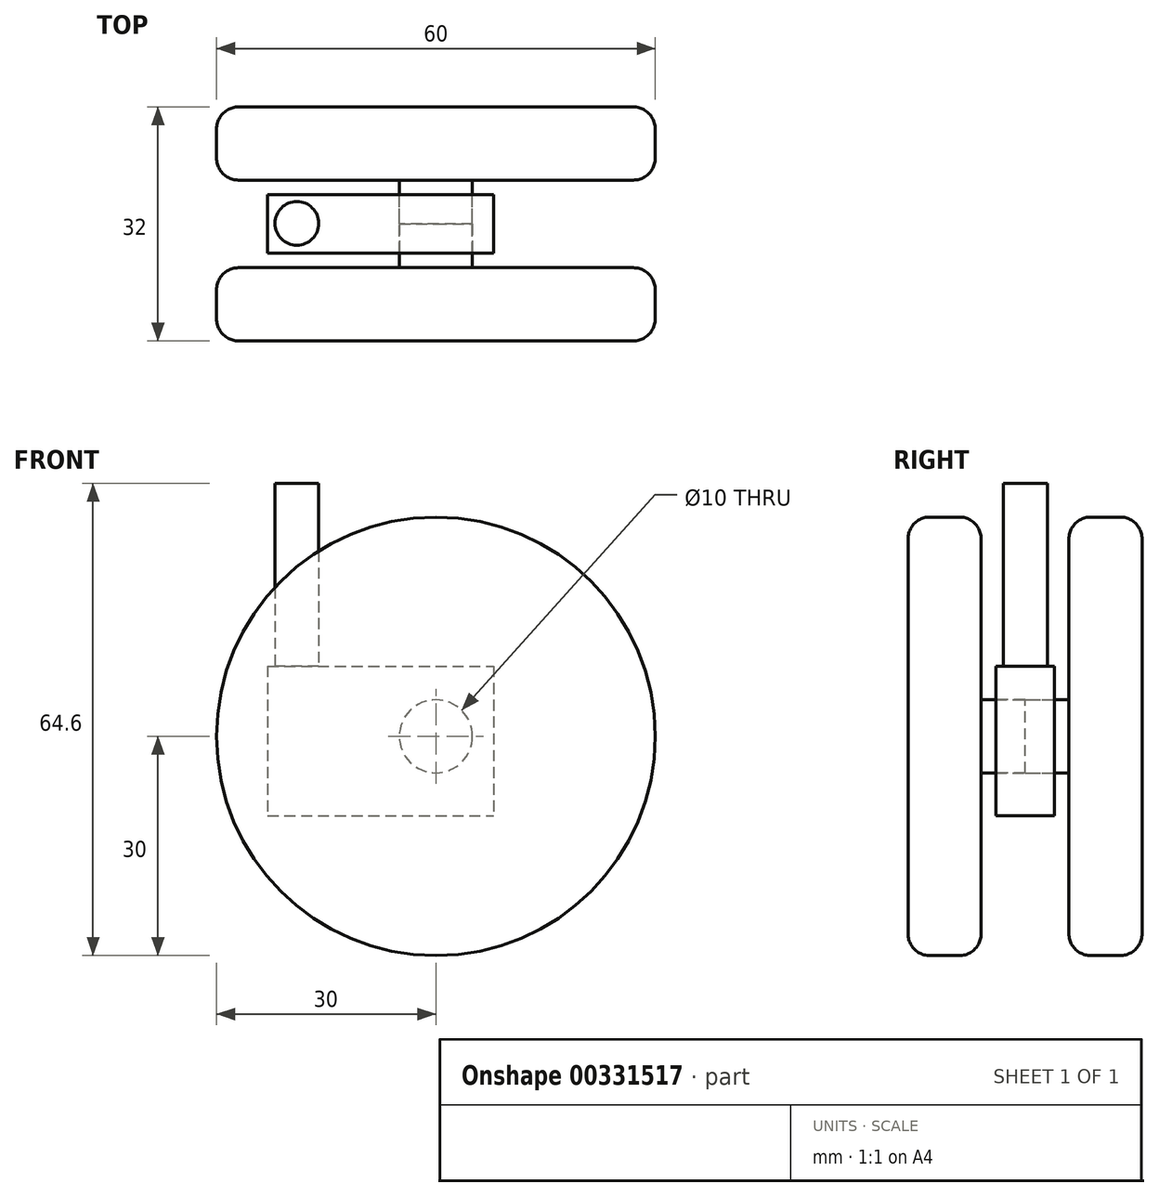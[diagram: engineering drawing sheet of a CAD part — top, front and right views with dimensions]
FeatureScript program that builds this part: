
annotation { "Feature Type Name" : "Feature", "Feature Type Description" : "" }
export const myFeature = defineFeature(function(context is Context, id is Id, definition is map)
    precondition{}
    {
        {
            var Q0;
            Q0=qCreatedBy(makeId("Front.planeOp"),FACE);
            var sketch = newSketch(context, id + "F0", { "sketchPlane" : qUnion([Q0])});
            skCircle(sketch, "E0", {"center": v(0, 0) * mm, "radius": 30 * mm});
            skSolve(sketch);
        }
        {
            var Q0;
            Q0=makeQuery(id+"F0.imprint","IMPRINT",FACE,{"disambiguationData":[TD([[makeQuery(id+"F0.imprint","IMPRINT",EDGE,{"derivedFrom":sQuery(id+"F0.wireOp",EDGE,"E0")}),1.0]])]});
            extrude(context, id + "F1", {"entities" : qUnion([Q0]), "depth" : 10 * mm});
        }
        {
            var Q0;
            Q0=makeQuery(id+"F1.opExtrude","CAP_EDGE",EDGE,{"disambiguationData":[OSD([sQuery(id+"F0.wireOp",EDGE,"E0")])],"isStart":false});
            var Q1;
            Q1=makeQuery(id+"F1.opExtrude","CAP_EDGE",EDGE,{"disambiguationData":[OSD([sQuery(id+"F0.wireOp",EDGE,"E0")])],"isStart":true});
            fillet(context, id + "F2", {"entities" : qUnion([Q0, Q1]), "radius" : 3 * mm, "tangentPropagation" : true, "allowEdgeOverflow" : false});
        }
        {
            var Q0;
            Q0=makeQuery(id+"F1.opExtrude","CAP_FACE",FACE,{"disambiguationData":[OSD([sQuery(id+"F0.wireOp",EDGE,"E0")])],"isStart":false});
            var sketch = newSketch(context, id + "F3", { "sketchPlane" : qUnion([Q0])});
            skCircle(sketch, "E1", {"center": v(0, 0) * mm, "radius": 5 * mm});
            skSolve(sketch);
        }
        {
            var Q0;
            Q0=makeQuery(id+"F3.imprint","IMPRINT",FACE,{"disambiguationData":[TD([[makeQuery(id+"F3.imprint","IMPRINT",EDGE,{"derivedFrom":sQuery(id+"F3.wireOp",EDGE,"E1")}),1.0]])]});
            extrude(context, id + "F4", {"entities" : qUnion([Q0]), "operationType" : NewBodyOperationType.ADD, "depth" : 6 * mm});
        }
        {
            var Q0;
            Q0=makeQuery(id+"F1.opExtrude","SWEPT_BODY",BODY,{"disambiguationData":[OSD([sQuery(id+"F0.wireOp",EDGE,"E0")])]});
            var Q1;
            Q1=makeQuery(id+"F4.opExtrude","CAP_FACE",FACE,{"disambiguationData":[OSD([sQuery(id+"F3.wireOp",EDGE,"E1")])],"isStart":false});
            mirror(context, id + "F5", {"entities" : qUnion([Q0]), "mirrorPlane" : qUnion([Q1])});
        }
        {
            var Q0;
            Q0=makeQuery(id+"F4.opExtrude","CAP_FACE",FACE,{"disambiguationData":[OSD([sQuery(id+"F3.wireOp",EDGE,"E1")])],"isStart":false});
            var sketch = newSketch(context, id + "F6", { "sketchPlane" : qUnion([Q0])});
            skLineSegment(sketch, "E2.bottom", {"start": v(-23.02, 9.6) * mm, "end": v(7.88, 9.6) * mm});
            skLineSegment(sketch, "E2.top", {"start": v(-23.02, -10.83) * mm, "end": v(7.88, -10.83) * mm});
            skLineSegment(sketch, "E2.left", {"start": v(-23.02, 9.6) * mm, "end": v(-23.02, -10.83) * mm});
            skLineSegment(sketch, "E2.right", {"start": v(7.88, 9.6) * mm, "end": v(7.88, -10.83) * mm});
            skSolve(sketch);
        }
        {
            var Q0;
            Q0=makeQuery(id+"F6.imprint","IMPRINT",FACE,{"disambiguationData":[TD([[makeQuery(id+"F6.imprint","IMPRINT",EDGE,{"derivedFrom":sQuery(id+"F6.wireOp",EDGE,"E2.bottom")}),-1.0]])]});
            extrude(context, id + "F7", {"entities" : qUnion([Q0]), "endBound" : BoundingType.SYMMETRIC, "depth" : 8 * mm});
        }
        {
            var Q0;
            Q0=makeQuery(id+"F7.opExtrude","SWEPT_FACE",FACE,{"disambiguationData":[OSD([sQuery(id+"F6.wireOp",EDGE,"E2.bottom")])]});
            var sketch = newSketch(context, id + "F8", { "sketchPlane" : qUnion([Q0])});
            skLineSegment(sketch, "E3", {"start": v(-19.02, -12) * mm, "end": v(-19.02, -20) * mm, "construction": true});
            skCircle(sketch, "E4", {"center": v(-19.02, -15.93) * mm, "radius": 3 * mm});
            skSolve(sketch);
        }
        {
            var Q0;
            Q0=makeQuery(id+"F8.imprint","IMPRINT",FACE,{"disambiguationData":[TD([[makeQuery(id+"F8.imprint","IMPRINT",EDGE,{"derivedFrom":sQuery(id+"F8.wireOp",EDGE,"E4")}),1.0]])]});
            extrude(context, id + "F9", {"entities" : qUnion([Q0]), "operationType" : NewBodyOperationType.ADD, "depth" : 25 * mm});
        }
    });
